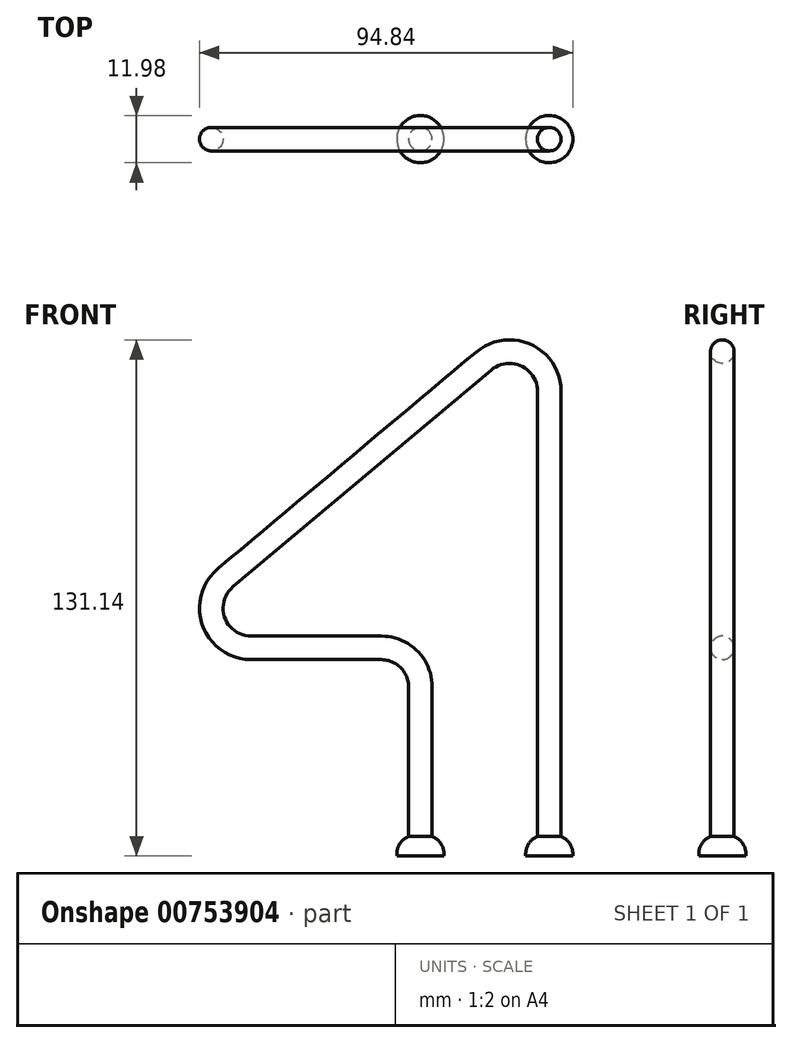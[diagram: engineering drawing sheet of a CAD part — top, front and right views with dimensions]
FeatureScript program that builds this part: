
annotation { "Feature Type Name" : "Feature", "Feature Type Description" : "" }
export const myFeature = defineFeature(function(context is Context, id is Id, definition is map)
    precondition{}
    {
        {
            var Q0;
            Q0=qCreatedBy(makeId("Front.planeOp"),FACE);
            var sketch = newSketch(context, id + "F0", { "sketchPlane" : qUnion([Q0])});
            skLineSegment(sketch, "E0", {"start": v(51.94, -22.18) * mm, "end": v(51.94, 95.87) * mm});
            skLineSegment(sketch, "E1", {"start": v(35.52, 103.53) * mm, "end": v(-30.15, 48.45) * mm});
            skLineSegment(sketch, "E2", {"start": v(-23.72, 30.8) * mm, "end": v(9.4, 30.8) * mm});
            skLineSegment(sketch, "E3", {"start": v(19.4, 20.8) * mm, "end": v(19.4, -22.18) * mm});
            skPoint(sketch, "E4.visualSharp", {"position": v(-51.2, 30.8) * mm});
            skArc(sketch, "E4.filletArc", {"start": v(-30.15, 48.45) * mm, "mid": v(-33.12, 37.37) * mm, "end": v(-23.72, 30.8) * mm});
            skPoint(sketch, "E5.visualSharp", {"position": v(51.94, 117.31) * mm});
            skArc(sketch, "E5.filletArc", {"start": v(51.94, 95.87) * mm, "mid": v(46.17, 104.93) * mm, "end": v(35.52, 103.53) * mm});
            skPoint(sketch, "E6.visualSharp", {"position": v(19.4, 30.8) * mm});
            skArc(sketch, "E6.filletArc", {"start": v(19.4, 20.8) * mm, "mid": v(16.47, 27.86) * mm, "end": v(9.4, 30.8) * mm});
            skSolve(sketch);
        }
        {
            var Q0;
            Q0=sQuery(id+"F0.wireOp",VERTEX,"E0.start");
            var Q1;
            Q1=sQuery(id+"F0.wireOp",EDGE,"E0");
            cPlane(context, id + "F1", {"entities" : qUnion([Q0, Q1]), "cplaneType" : CPlaneType.LINE_POINT, "offset" : 25 * mm, "width" : 150 * mm, "height" : 150 * mm});
        }
        {
            var Q0;
            Q0=qCreatedBy(id+"F1.planeOp",FACE);
            var sketch = newSketch(context, id + "F2", { "sketchPlane" : qUnion([Q0])});
            skCircle(sketch, "E7", {"center": v(52.04, 0) * mm, "radius": 3 * mm});
            skSolve(sketch);
        }
        {
            var Q0;
            Q0=makeQuery(id+"F2.imprint","IMPRINT",FACE,{"disambiguationData":[TD([[makeQuery(id+"F2.imprint","IMPRINT",EDGE,{"derivedFrom":sQuery(id+"F2.wireOp",EDGE,"E7")}),1.0]])]});
            var Q1;
            Q1=sQuery(id+"F0.wireOp",EDGE,"E0");
            var Q2;
            Q2=sQuery(id+"F0.wireOp",EDGE,"E5.filletArc");
            var Q3;
            Q3=sQuery(id+"F0.wireOp",EDGE,"E1");
            var Q4;
            Q4=sQuery(id+"F0.wireOp",EDGE,"E4.filletArc");
            var Q5;
            Q5=sQuery(id+"F0.wireOp",EDGE,"E2");
            var Q6;
            Q6=sQuery(id+"F0.wireOp",EDGE,"E6.filletArc");
            var Q7;
            Q7=sQuery(id+"F0.wireOp",EDGE,"E3");
            sweep(context, id + "F3", {"profiles" : qUnion([Q0]), "path" : qUnion([Q1, Q2, Q3, Q4, Q5, Q6, Q7])});
        }
        {
            var Q0;
            Q0=qCreatedBy(id+"F1.planeOp",FACE);
            var sketch = newSketch(context, id + "F4", { "sketchPlane" : qUnion([Q0])});
            skCircle(sketch, "E8.0", {"center": v(52.04, 0) * mm, "radius": 6 * mm});
            skCircle(sketch, "E9.0", {"center": v(19.3, 0) * mm, "radius": 6 * mm});
            skSolve(sketch);
        }
        {
            var Q0;
            Q0=makeQuery(id+"F4.imprint","IMPRINT",FACE,{"disambiguationData":[TD([[makeQuery(id+"F4.imprint","IMPRINT",EDGE,{"derivedFrom":sQuery(id+"F4.wireOp",EDGE,"E8.0")}),1.0]])]});
            var Q1;
            Q1=makeQuery(id+"F4.imprint","IMPRINT",FACE,{"disambiguationData":[TD([[makeQuery(id+"F4.imprint","IMPRINT",EDGE,{"derivedFrom":sQuery(id+"F4.wireOp",EDGE,"E9.0")}),1.0]])]});
            extrude(context, id + "F5", {"entities" : qUnion([Q0, Q1]), "operationType" : NewBodyOperationType.ADD, "depth" : 5 * mm, "offsetDistance" : 25 * mm});
        }
        {
            var Q0;
            Q0=makeQuery(id+"F5.opExtrude","CAP_EDGE",EDGE,{"disambiguationData":[OSD([sQuery(id+"F4.wireOp",EDGE,"E8.0")])],"isStart":false});
            var Q1;
            Q1=makeQuery(id+"F5.opExtrude","CAP_EDGE",EDGE,{"disambiguationData":[OSD([sQuery(id+"F4.wireOp",EDGE,"E9.0")])],"isStart":false});
            fillet(context, id + "F6", {"entities" : qUnion([Q0, Q1]), "radius" : 5 * mm, "tangentPropagation" : true, "allowEdgeOverflow" : false});
        }
    });
